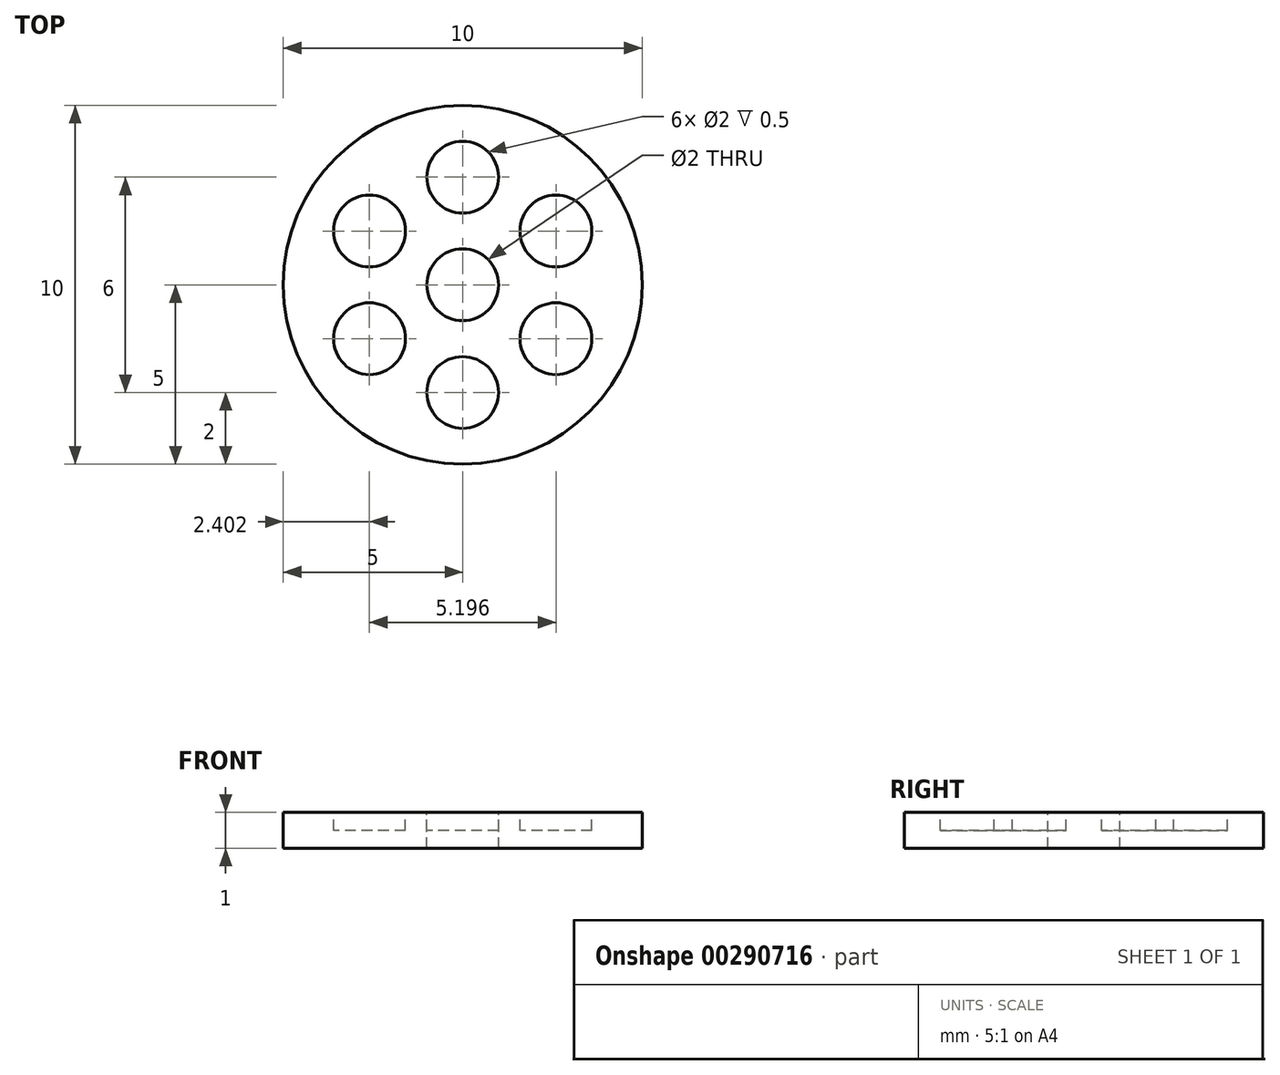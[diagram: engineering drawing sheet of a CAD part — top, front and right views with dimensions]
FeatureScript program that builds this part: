
annotation { "Feature Type Name" : "Feature", "Feature Type Description" : "" }
export const myFeature = defineFeature(function(context is Context, id is Id, definition is map)
    precondition{}
    {
        {
            var Q0;
            Q0=qCreatedBy(makeId("Top.planeOp"),FACE);
            var sketch = newSketch(context, id + "F0", { "sketchPlane" : qUnion([Q0])});
            skCircle(sketch, "E0", {"center": v(0, 0) * mm, "radius": 5 * mm});
            skSolve(sketch);
        }
        {
            var Q0;
            Q0=makeQuery(id+"F0.imprint","IMPRINT",FACE,{"disambiguationData":[TD([[makeQuery(id+"F0.imprint","IMPRINT",EDGE,{"derivedFrom":sQuery(id+"F0.wireOp",EDGE,"E0")}),1.0]])]});
            var Q1;
            Q1=sQuery(id+"F0.wireOp",EDGE,"E0");
            extrude(context, id + "F1", {"entities" : qUnion([Q0]), "surfaceEntities" : qUnion([Q1]), "depth" : 1 * mm});
        }
        {
            var Q0;
            Q0=makeQuery(id+"F1.opExtrude","CAP_FACE",FACE,{"disambiguationData":[OSD([sQuery(id+"F0.wireOp",EDGE,"E0")])],"isStart":false});
            var sketch = newSketch(context, id + "F2", { "sketchPlane" : qUnion([Q0])});
            skLineSegment(sketch, "E1", {"start": v(0, 0) * mm, "end": v(0, 3) * mm, "construction": true});
            skCircle(sketch, "E2", {"center": v(0, 3) * mm, "radius": 1 * mm});
            skCircle(sketch, "E3.1.0", {"center": v(-2.6, 1.5) * mm, "radius": 1 * mm});
            skCircle(sketch, "E3.2.0", {"center": v(-2.6, -1.5) * mm, "radius": 1 * mm});
            skPoint(sketch, "E3.center", {"position": v(0, 0) * mm});
            skCircle(sketch, "E4.1.3.0", {"center": v(0, -3) * mm, "radius": 1 * mm});
            skCircle(sketch, "E4.1.4.0", {"center": v(2.6, -1.5) * mm, "radius": 1 * mm});
            skCircle(sketch, "E5.1.5.0", {"center": v(2.6, 1.5) * mm, "radius": 1 * mm});
            skSolve(sketch);
        }
        {
            var Q0;
            Q0 = qSketchRegion(id + "F2", true);
            extrude(context, id + "F3", {"entities" : qUnion([Q0]), "operationType" : NewBodyOperationType.REMOVE, "oppositeDirection" : true, "depth" : 0.5 * mm});
        }
        {
            var Q0;
            Q0=makeQuery(id+"F1.opExtrude","CAP_FACE",FACE,{"disambiguationData":[OSD([sQuery(id+"F0.wireOp",EDGE,"E0")])],"isStart":false});
            var sketch = newSketch(context, id + "F4", { "sketchPlane" : qUnion([Q0])});
            skCircle(sketch, "E6", {"center": v(0, 0) * mm, "radius": 1 * mm});
            skSolve(sketch);
        }
        {
            var Q0;
            Q0 = qSketchRegion(id + "F4", true);
            extrude(context, id + "F5", {"entities" : qUnion([Q0]), "operationType" : NewBodyOperationType.REMOVE, "oppositeDirection" : true, "depth" : 1 * mm});
        }
    });
